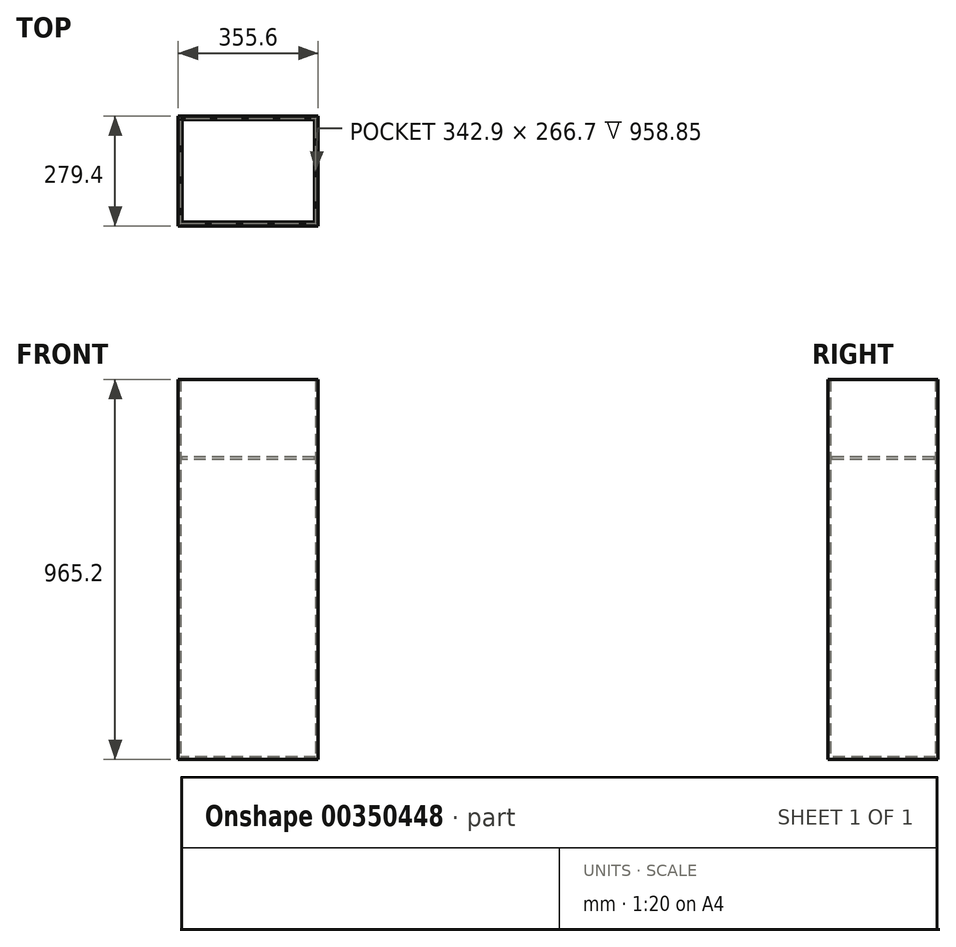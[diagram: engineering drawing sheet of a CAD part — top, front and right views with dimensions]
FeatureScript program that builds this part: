
annotation { "Feature Type Name" : "Feature", "Feature Type Description" : "" }
export const myFeature = defineFeature(function(context is Context, id is Id, definition is map)
    precondition{}
    {
        {
            var Q0;
            Q0=qCreatedBy(makeId("Top.planeOp"),FACE);
            var sketch = newSketch(context, id + "F0", { "sketchPlane" : qUnion([Q0])});
            skLineSegment(sketch, "E0.bottom", {"start": v(177.8, 139.7) * mm, "end": v(-177.8, 139.7) * mm});
            skLineSegment(sketch, "E0.top", {"start": v(177.8, -139.7) * mm, "end": v(-177.8, -139.7) * mm});
            skLineSegment(sketch, "E0.left", {"start": v(177.8, 139.7) * mm, "end": v(177.8, -139.7) * mm});
            skLineSegment(sketch, "E0.right", {"start": v(-177.8, 139.7) * mm, "end": v(-177.8, -139.7) * mm});
            skPoint(sketch, "E0.middle", {"position": v(0, 0) * mm});
            skSolve(sketch);
        }
        {
            var Q0;
            Q0=makeQuery(id+"F0.imprint","IMPRINT",FACE,{"disambiguationData":[TD([[makeQuery(id+"F0.imprint","IMPRINT",EDGE,{"derivedFrom":sQuery(id+"F0.wireOp",EDGE,"E0.bottom")}),1.0]])]});
            extrude(context, id + "F1", {"entities" : qUnion([Q0]), "depth" : 965.2 * mm});
        }
        {
            var Q0;
            Q0=makeQuery(id+"F1.opExtrude","CAP_FACE",FACE,{"disambiguationData":[OSD([sQuery(id+"F0.wireOp",EDGE,"E0.bottom"),sQuery(id+"F0.wireOp",EDGE,"E0.top"),sQuery(id+"F0.wireOp",EDGE,"E0.left"),sQuery(id+"F0.wireOp",EDGE,"E0.right")])],"isStart":false});
            shell(context, id + "F2", {"entities" : qUnion([Q0]), "thickness" : 6.35 * mm});
        }
        {
            var Q0;
            Q0=makeQuery(id+"F1.opExtrude","CAP_FACE",FACE,{"disambiguationData":[OSD([sQuery(id+"F0.wireOp",EDGE,"E0.bottom"),sQuery(id+"F0.wireOp",EDGE,"E0.top"),sQuery(id+"F0.wireOp",EDGE,"E0.left"),sQuery(id+"F0.wireOp",EDGE,"E0.right")])],"isStart":false});
            var sketch = newSketch(context, id + "F3", { "sketchPlane" : qUnion([Q0])});
            skLineSegment(sketch, "E1.bottom", {"start": v(168.27, 130.18) * mm, "end": v(-168.28, 130.18) * mm});
            skLineSegment(sketch, "E1.top", {"start": v(168.28, -130.18) * mm, "end": v(-168.27, -130.18) * mm});
            skLineSegment(sketch, "E1.left", {"start": v(168.27, 130.18) * mm, "end": v(168.28, -130.18) * mm});
            skLineSegment(sketch, "E1.right", {"start": v(-168.28, 130.18) * mm, "end": v(-168.27, -130.18) * mm});
            skPoint(sketch, "E1.middle", {"position": v(0, 0) * mm});
            skSolve(sketch);
        }
        {
            var Q0;
            Q0=makeQuery(id+"F3.imprint","IMPRINT",FACE,{"disambiguationData":[TD([[makeQuery(id+"F3.imprint","IMPRINT",EDGE,{"derivedFrom":sQuery(id+"F3.wireOp",EDGE,"E1.bottom")}),1.0]])]});
            extrude(context, id + "F4", {"entities" : qUnion([Q0]), "oppositeDirection" : true, "depth" : 203.2 * mm, "hasSecondDirection" : true, "secondDirectionOppositeDirection" : true, "secondDirectionDepth" : 196.85 * mm});
        }
    });
